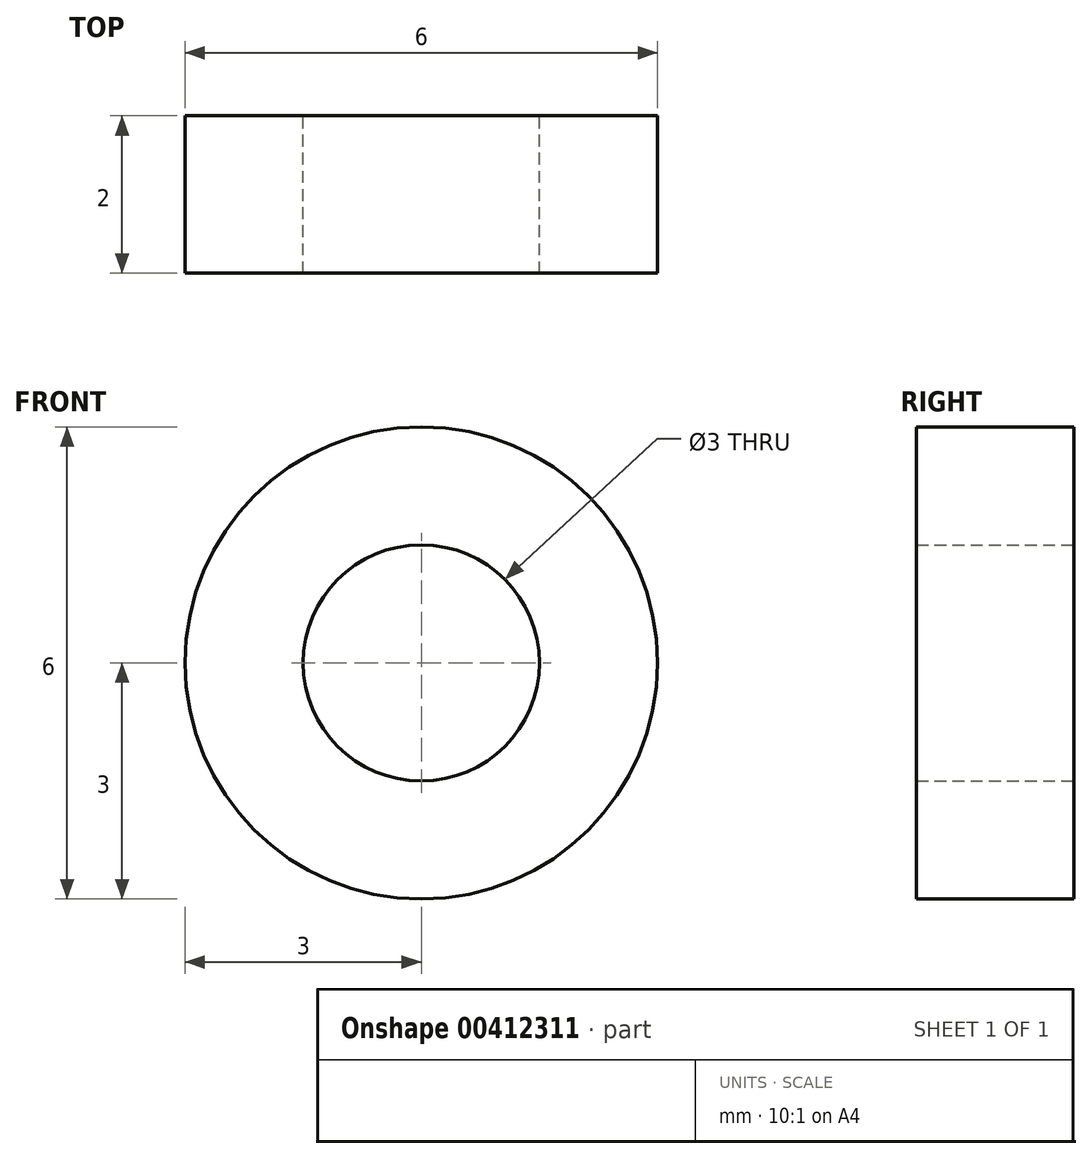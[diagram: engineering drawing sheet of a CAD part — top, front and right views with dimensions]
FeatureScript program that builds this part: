
annotation { "Feature Type Name" : "Feature", "Feature Type Description" : "" }
export const myFeature = defineFeature(function(context is Context, id is Id, definition is map)
    precondition{}
    {
        {
            var Q0;
            Q0=qCreatedBy(makeId("Front.planeOp"),FACE);
            var sketch = newSketch(context, id + "F0", { "sketchPlane" : qUnion([Q0])});
            skCircle(sketch, "E0", {"center": v(0, 0) * mm, "radius": 1.5 * mm});
            skCircle(sketch, "E1", {"center": v(0, 0) * mm, "radius": 3 * mm});
            skSolve(sketch);
        }
        {
            var Q0;
            Q0 = qSketchRegion(id + "F0", true);
            extrude(context, id + "F1", {"entities" : qUnion([Q0]), "depth" : 2 * mm});
        }
    });
